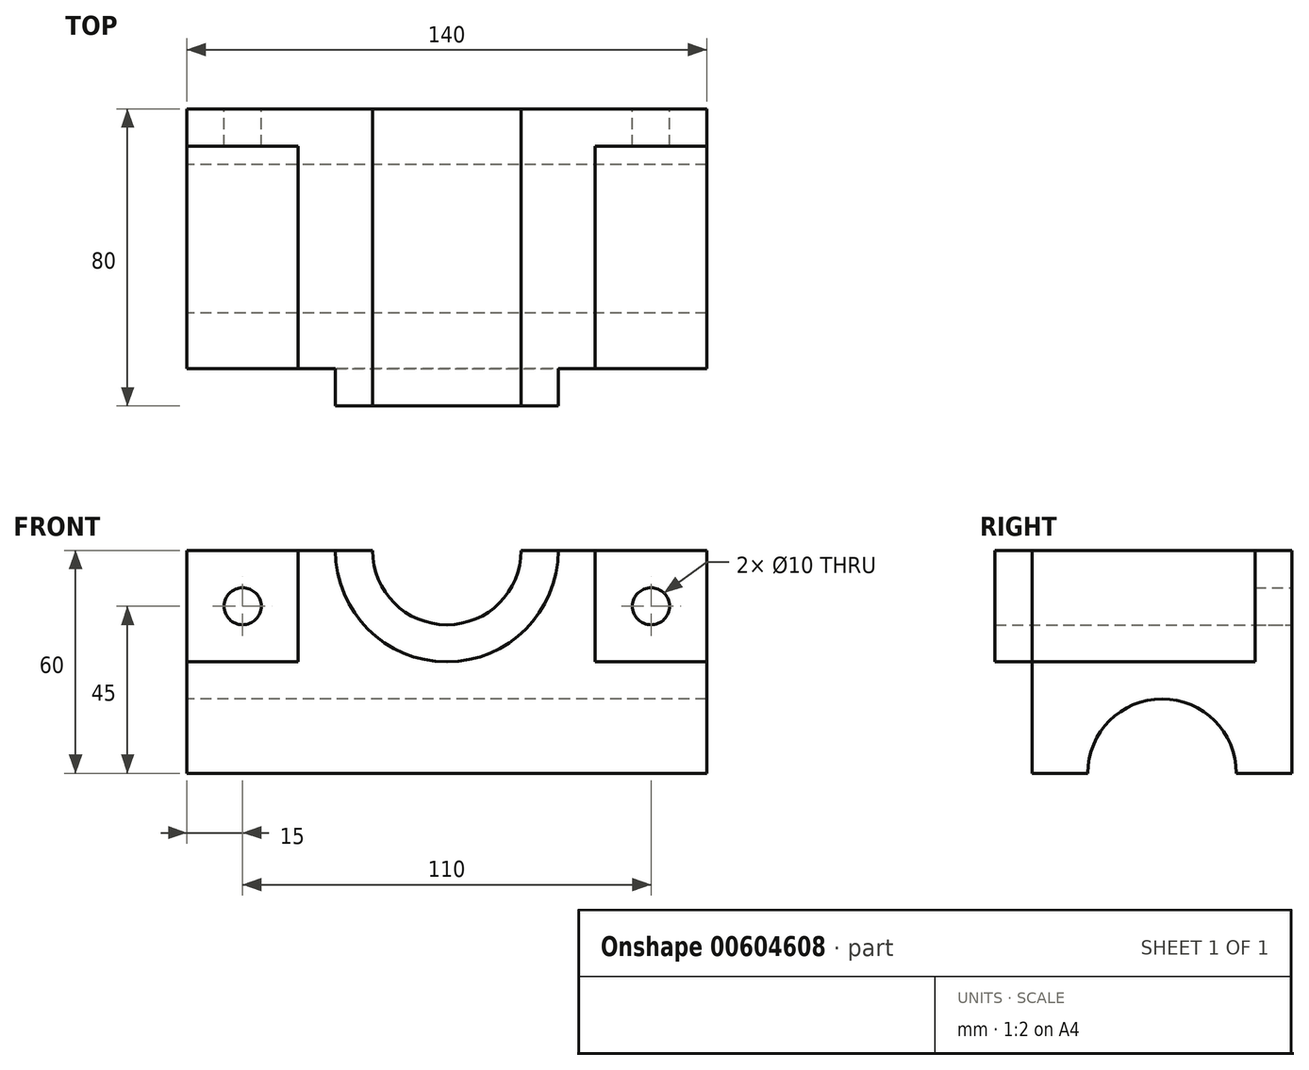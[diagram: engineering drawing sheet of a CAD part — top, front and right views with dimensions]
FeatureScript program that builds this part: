
annotation { "Feature Type Name" : "Feature", "Feature Type Description" : "" }
export const myFeature = defineFeature(function(context is Context, id is Id, definition is map)
    precondition{}
    {
        {
            var Q0;
            Q0=qCreatedBy(makeId("Front.planeOp"),FACE);
            var sketch = newSketch(context, id + "F0", { "sketchPlane" : qUnion([Q0])});
            skLineSegment(sketch, "E0.bottom", {"start": v(-20, 60) * mm, "end": v(-70, 60) * mm});
            skLineSegment(sketch, "E0.top", {"start": v(0, 0) * mm, "end": v(-70, 0) * mm});
            skLineSegment(sketch, "E0.left", {"start": v(0, 40) * mm, "end": v(0, 0) * mm});
            skLineSegment(sketch, "E0.right", {"start": v(-70, 60) * mm, "end": v(-70, 0) * mm});
            skArc(sketch, "E1", {"start": v(-20, 60) * mm, "mid": v(-14.14, 45.86) * mm, "end": v(0, 40) * mm});
            skLineSegment(sketch, "E2", {"start": v(-70, 30) * mm, "end": v(-40, 30) * mm});
            skLineSegment(sketch, "E3", {"start": v(-40, 30) * mm, "end": v(-40, 60) * mm});
            skArc(sketch, "E4", {"start": v(-30, 60) * mm, "mid": v(-21.21, 38.79) * mm, "end": v(0, 30) * mm});
            skLineSegment(sketch, "E5", {"start": v(-55, 30) * mm, "end": v(-55, 60) * mm, "construction": true});
            skLineSegment(sketch, "E6", {"start": v(-40, 45) * mm, "end": v(-70, 45) * mm, "construction": true});
            skCircle(sketch, "E7", {"center": v(-55, 45) * mm, "radius": 5 * mm});
            skSolve(sketch);
        }
        {
            var Q0;
            {var subQ1=sQuery(id+"F0.wireOp",EDGE,"E0.top");Q0=makeQuery(id+"F0.imprint","IMPRINT",FACE,{"disambiguationData":[TD([[makeQuery(id+"F0.imprint","IMPRINT",EDGE,{"derivedFrom":subQ1}),-1.0]])]});}
            extrude(context, id + "F1", {"entities" : qUnion([Q0]), "depth" : 70 * mm, "offsetDistance" : 25 * mm});
        }
        {
            var Q0;
            {var subQ1=sQuery(id+"F0.wireOp",EDGE,"E2");Q0=makeQuery(id+"F0.imprint","IMPRINT",FACE,{"disambiguationData":[TD([[makeQuery(id+"F0.imprint","IMPRINT",EDGE,{"derivedFrom":subQ1}),1.0]])]});}
            extrude(context, id + "F2", {"entities" : qUnion([Q0]), "operationType" : NewBodyOperationType.ADD, "depth" : 10 * mm, "offsetDistance" : 25 * mm});
        }
        {
            var Q0;
            {var subQ0=sQuery(id+"F0.wireOp",EDGE,"E1");Q0=makeQuery(id+"F0.imprint","IMPRINT",FACE,{"disambiguationData":[TD([[makeQuery(id+"F0.imprint","IMPRINT",EDGE,{"derivedFrom":subQ0}),-1.0]])]});}
            extrude(context, id + "F3", {"entities" : qUnion([Q0]), "operationType" : NewBodyOperationType.ADD, "depth" : 80 * mm, "offsetDistance" : 25 * mm});
        }
        {
            var Q0;
            Q0=makeQuery(id+"F1.opExtrude","SWEPT_BODY",BODY,{"disambiguationData":[OSD([sQuery(id+"F0.wireOp",EDGE,"E0.bottom"),sQuery(id+"F0.wireOp",EDGE,"E0.top"),sQuery(id+"F0.wireOp",EDGE,"E0.left"),sQuery(id+"F0.wireOp",EDGE,"E0.right"),sQuery(id+"F0.wireOp",EDGE,"E2"),sQuery(id+"F0.wireOp",EDGE,"E3"),sQuery(id+"F0.wireOp",EDGE,"E4")])]});
            var Q1;
            Q1=qCreatedBy(makeId("Right.planeOp"),FACE);
            mirror(context, id + "F4", {"operationType" : NewBodyOperationType.ADD, "entities" : qUnion([Q0]), "mirrorPlane" : qUnion([Q1])});
        }
        {
            var Q0;
            {var subQ0=sQuery(id+"F0.wireOp",EDGE,"E0.right");Q0=makeQuery(id+"F2.boolean.opBoolean","MERGE",FACE,{"derivedFrom":[makeQuery(id+"F1.opExtrude","SWEPT_FACE",FACE,{"disambiguationData":[OSD([subQ0])]}),makeQuery(id+"F2.opExtrude","SWEPT_FACE",FACE,{"disambiguationData":[OSD([subQ0])]})]});}
            var sketch = newSketch(context, id + "F5", { "sketchPlane" : qUnion([Q0])});
            skCircle(sketch, "E8", {"center": v(35, 0) * mm, "radius": 20 * mm});
            skSolve(sketch);
        }
        {
            var Q0;
            {var subQ0=sQuery(id+"F5.wireOp",EDGE,"E8");var subQ1=makeQuery(id+"F1.opExtrude","SWEPT_EDGE",EDGE,{"disambiguationData":[OSD([sQuery(id+"F0.wireOp",EDGE,"E0.top"),sQuery(id+"F0.wireOp",EDGE,"E0.right")])]});var subQ2=makeQuery(id+"F5.imprint","INTERSECT",VERTEX,{"disambiguationData":[OD(0.0)],"derivedFrom":[subQ1,subQ0]});Q0=makeQuery(id+"F5.imprint","IMPRINT",FACE,{"disambiguationData":[TD([[makeQuery(id+"F5.imprint","IMPRINT",EDGE,{"disambiguationData":[TD([[subQ2,1.0]])],"derivedFrom":subQ0}),1.0]])]});}
            extrude(context, id + "F6", {"entities" : qUnion([Q0]), "operationType" : NewBodyOperationType.REMOVE, "endBound" : BoundingType.THROUGH_ALL, "oppositeDirection" : true, "depth" : 25 * mm, "offsetDistance" : 25 * mm});
        }
    });
